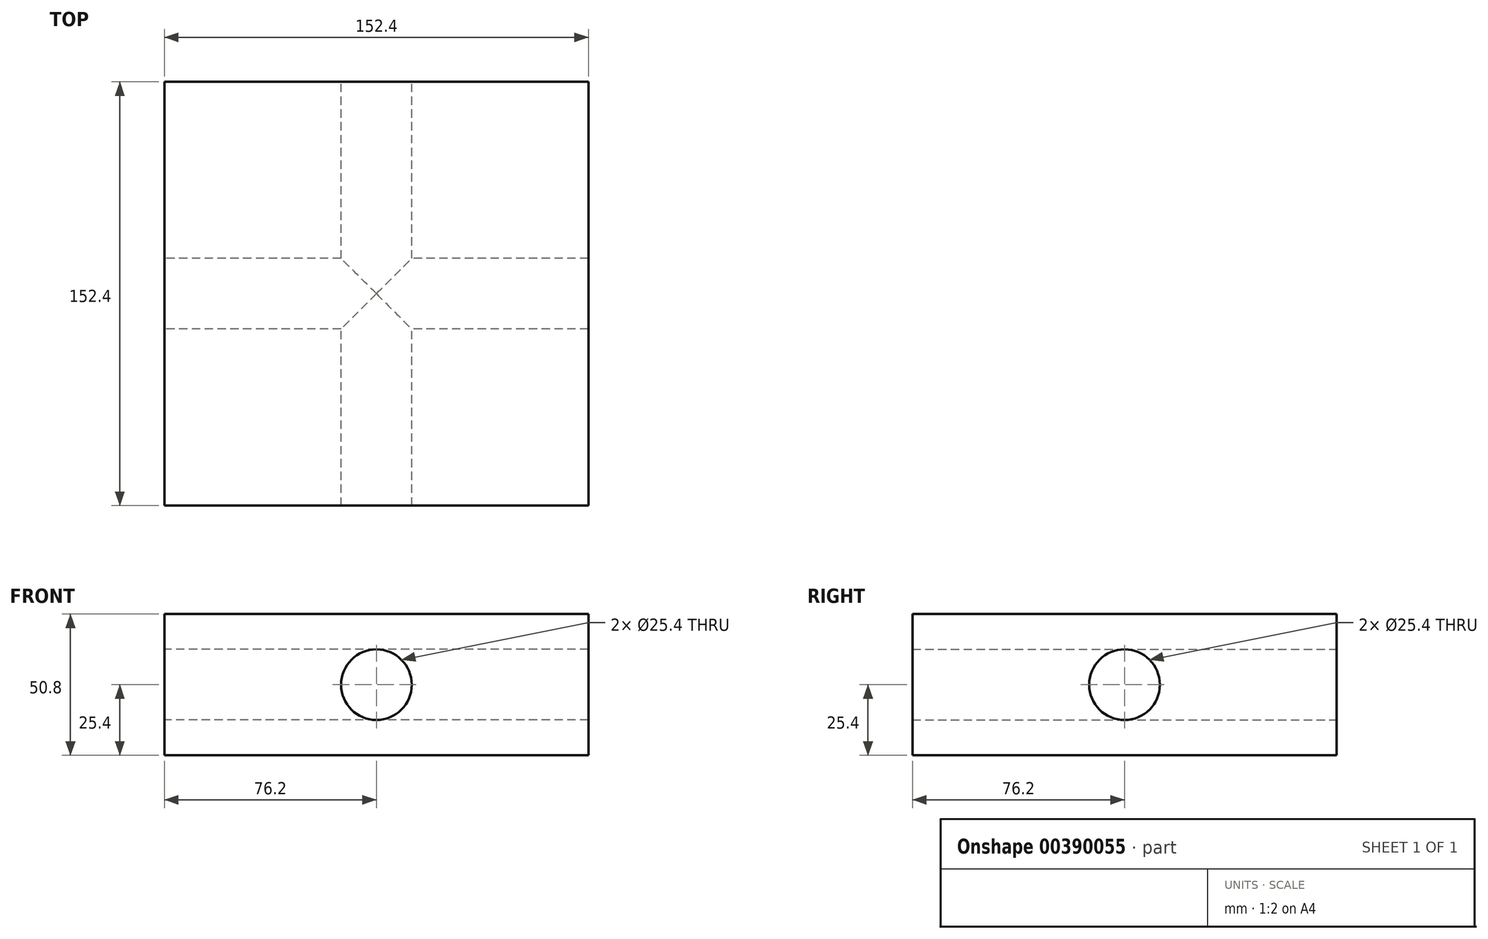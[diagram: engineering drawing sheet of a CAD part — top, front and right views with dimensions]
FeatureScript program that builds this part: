
annotation { "Feature Type Name" : "Feature", "Feature Type Description" : "" }
export const myFeature = defineFeature(function(context is Context, id is Id, definition is map)
    precondition{}
    {
        {
            var Q0;
            Q0=qCreatedBy(makeId("Top.planeOp"),FACE);
            var sketch = newSketch(context, id + "F0", { "sketchPlane" : qUnion([Q0])});
            skLineSegment(sketch, "E0.bottom", {"start": v(76.2, -76.2) * mm, "end": v(-76.2, -76.2) * mm});
            skLineSegment(sketch, "E0.top", {"start": v(76.2, 76.2) * mm, "end": v(-76.2, 76.2) * mm});
            skLineSegment(sketch, "E0.left", {"start": v(76.2, -76.2) * mm, "end": v(76.2, 76.2) * mm});
            skLineSegment(sketch, "E0.right", {"start": v(-76.2, -76.2) * mm, "end": v(-76.2, 76.2) * mm});
            skPoint(sketch, "E0.middle", {"position": v(0, 0) * mm});
            skSolve(sketch);
        }
        {
            var Q0;
            Q0=makeQuery(id+"F0.imprint","IMPRINT",FACE,{"disambiguationData":[TD([[makeQuery(id+"F0.imprint","IMPRINT",EDGE,{"derivedFrom":sQuery(id+"F0.wireOp",EDGE,"E0.bottom")}),-1.0]])]});
            extrude(context, id + "F1", {"entities" : qUnion([Q0]), "depth" : 50.8 * mm});
        }
        {
            var Q0;
            Q0=makeQuery(id+"F1.opExtrude","SWEPT_FACE",FACE,{"disambiguationData":[OSD([sQuery(id+"F0.wireOp",EDGE,"E0.right")])]});
            var sketch = newSketch(context, id + "F2", { "sketchPlane" : qUnion([Q0])});
            skCircle(sketch, "E1", {"center": v(0, 25.4) * mm, "radius": 12.7 * mm});
            skPoint(sketch, "E1.centerSnap0", {"position": v(76.2, 25.4) * mm});
            skSolve(sketch);
        }
        {
            var Q0;
            Q0=makeQuery(id+"F1.opExtrude","SWEPT_FACE",FACE,{"disambiguationData":[OSD([sQuery(id+"F0.wireOp",EDGE,"E0.top")])]});
            var sketch = newSketch(context, id + "F3", { "sketchPlane" : qUnion([Q0])});
            skCircle(sketch, "E2", {"center": v(0, 25.4) * mm, "radius": 12.7 * mm});
            skPoint(sketch, "E2.centerSnap0", {"position": v(-76.2, 25.4) * mm});
            skPoint(sketch, "E2.centerSnap1", {"position": v(0, 50.8) * mm});
            skSolve(sketch);
        }
        {
            var Q0;
            Q0=makeQuery(id+"F3.imprint","IMPRINT",FACE,{"disambiguationData":[TD([[makeQuery(id+"F3.imprint","IMPRINT",EDGE,{"derivedFrom":sQuery(id+"F3.wireOp",EDGE,"E2")}),1.0]])]});
            extrude(context, id + "F4", {"entities" : qUnion([Q0]), "operationType" : NewBodyOperationType.REMOVE, "oppositeDirection" : true, "depth" : 152.4 * mm});
        }
        {
            var Q0;
            Q0=makeQuery(id+"F2.imprint","IMPRINT",FACE,{"disambiguationData":[TD([[makeQuery(id+"F2.imprint","IMPRINT",EDGE,{"derivedFrom":sQuery(id+"F2.wireOp",EDGE,"E1")}),1.0]])]});
            extrude(context, id + "F5", {"entities" : qUnion([Q0]), "operationType" : NewBodyOperationType.REMOVE, "oppositeDirection" : true, "depth" : 152.4 * mm});
        }
    });
